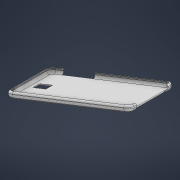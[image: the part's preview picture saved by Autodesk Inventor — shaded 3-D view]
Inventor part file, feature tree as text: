
AUTODESK INVENTOR PART (.ipt)
format: ipt  version: 2021 (Build 250183000, 183)  size: 4,002,304 bytes
history: native  units: mm
features: other x10, extrude x7, sketch x6, fillet x5, chamfer x4, thicken_offset x2, plane x2, surface_op x1
ambient origin geometry x8: Origin, YZ Plane, XZ Plane, XY Plane, X Axis, Y Axis, Z Axis, Center Point
bodies: Solid1 (feature_tree), Solid2 (feature_tree), Solid5 (feature_tree)
feature tree (37):
  other  "Blocks"
  extrude  "Extrusion1"  Depth=137.5mm
  fillet  "Fillet1"  [1 undecoded]
  fillet  "Fillet2"  Radius=9.9mm
  fillet  "Fillet3"  Radius=1.46mm
  thicken_offset  "Thicken1"
  chamfer  "Chamfer2"  [1 undecoded]
  extrude  "Extrusion2"  Depth=6.0mm TaperAngle=0.0deg
  plane  "Work Plane1"
  plane  "Work Plane2"
  other  "Ruled Surface6"
  surface_op  "Sculpt1"
  extrude  "Extrusion3"  Depth=6.0mm TaperAngle=0.0deg
  extrude  "Extrusion5"  Depth=2.0mm
  fillet  "Fillet5"  Radius=8.0mm
  thicken_offset  "Thicken2"
  chamfer  "Chamfer3"  Distance=8.0mm
  extrude  "Extrusion11"  Depth=8.0mm
  fillet  "Fillet6"  Radius=8.0mm
  chamfer  "Chamfer4"  Distance=5.9mm
  sketch  "Sketch17"  dims[d31=5.9mm d32=2.0mm]
  extrude  "Extrusion9"  Depth=24.5mm
  extrude  "Extrusion10"  Depth=19.0mm
  chamfer  "Chamfer5"  Distance=19.0mm
  sketch  "Sketch1"  dims[d0=208.4mm d1=137.5mm d3=0.0mm d4=9.9mm d7=1.46mm d8=0.8mm d18=0.0mm d19=0.0mm]
  sketch  "Sketch3"  dims[d20=53.5mm d22=6.0mm d23=0.0mm]
  sketch  "Sketch4"  dims[d28=5.9mm d29=6.0mm d30=0.0mm]
  other  "Srf7"
  other  "Ruled Surface7"
  other  "Srf8"
  sketch  "3D Sketch9"
  other  "Ruled Surface8"
  other  "Srf9"
  other  "pika"
  sketch  "Sketch18"  dims[d33=2.0mm d34=3.5mm d35=10.0mm d36=3.5mm d37=10.0mm d38=5.0mm d39=0.0mm d40=5.0mm d41=10.0mm d42=8.0mm d43=8.0mm d44=8.0mm d45=8.0mm d46=5.9mm d47=24.5mm d48=19.0mm d49=19.0mm d53=0.5mm d54=2.0mm d55=45.0deg d87=10.0mm d88=5.585054mm d89=10.0mm d90=0.0mm d91=10.0mm d92=45.0deg d108=2.0mm d109=1.0mm d110=1.0mm d111=1.0mm d112=2.0mm d113=45.0deg d116=0.2mm d117=0.0mm d118=0.2mm d119=0.0mm d120=22.0mm d121=8.0mm d122=52.75mm d123=52.75mm d124=0.0mm d125=0.0mm d126=1.0mm d127=1.5mm d128=2.46mm d129=45.0deg d130=0.2mm d131=2.0mm d132=45.0deg]
  other  "3D Intersection3"
  other  "pika:1"
note: 2 required parameter values undecoded (feature->parameter linkage not recoverable at this tier; creation-order binding heuristic only, values carry confidence <= 0.55)
